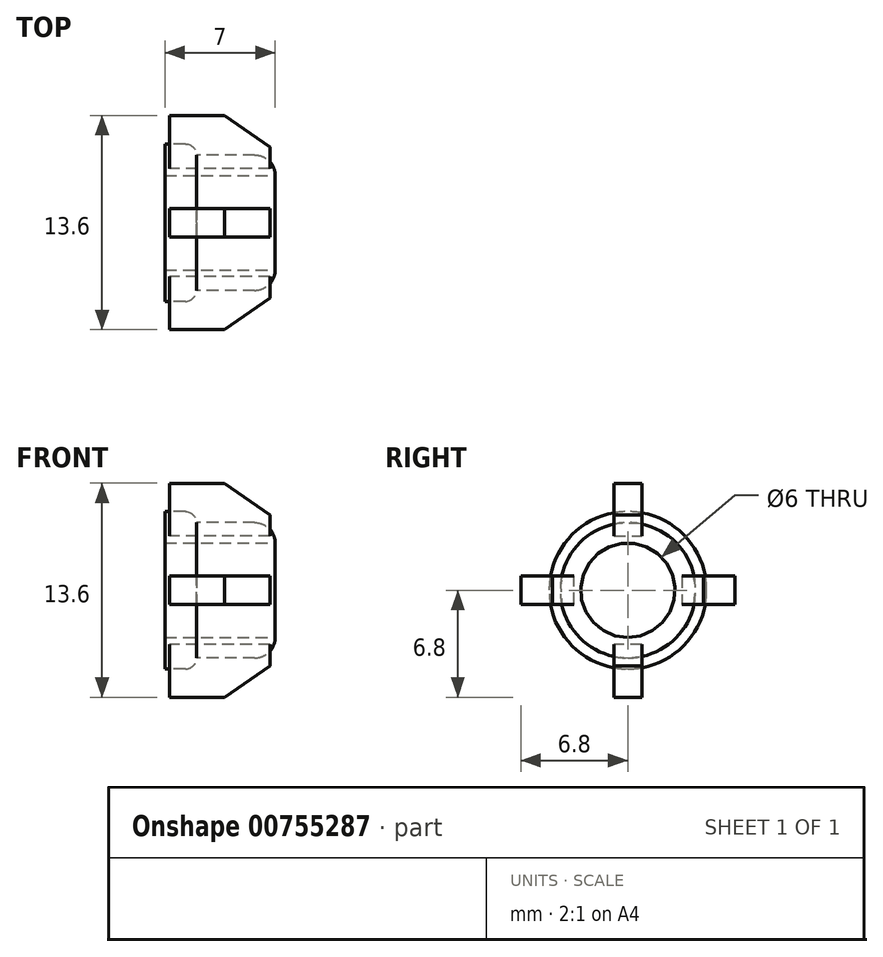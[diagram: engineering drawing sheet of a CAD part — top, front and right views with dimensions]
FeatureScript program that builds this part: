
annotation { "Feature Type Name" : "Feature", "Feature Type Description" : "" }
export const myFeature = defineFeature(function(context is Context, id is Id, definition is map)
    precondition{}
    {
        {
            var Q0;
            Q0=qCreatedBy(makeId("Right.planeOp"),FACE);
            var sketch = newSketch(context, id + "F0", { "sketchPlane" : qUnion([Q0])});
            skCircle(sketch, "E0", {"center": v(0, 0) * mm, "radius": 5 * mm});
            skSolve(sketch);
        }
        {
            var Q0;
            Q0=makeQuery(id+"F0.imprint","IMPRINT",FACE,{"disambiguationData":[TD([[makeQuery(id+"F0.imprint","IMPRINT",EDGE,{"derivedFrom":sQuery(id+"F0.wireOp",EDGE,"E0")}),1.0]])]});
            extrude(context, id + "F1", {"entities" : qUnion([Q0]), "depth" : 2 * mm, "offsetDistance" : 25 * mm});
        }
        {
            var Q0;
            Q0=makeQuery(id+"F1.opExtrude","CAP_FACE",FACE,{"disambiguationData":[OSD([sQuery(id+"F0.wireOp",EDGE,"E0")])],"isStart":false});
            fillet(context, id + "F2", {"entities" : qUnion([Q0]), "radius" : 0.7 * mm, "tangentPropagation" : true, "allowEdgeOverflow" : false});
        }
        {
            var Q0;
            Q0=makeQuery(id+"F1.opExtrude","CAP_FACE",FACE,{"disambiguationData":[OSD([sQuery(id+"F0.wireOp",EDGE,"E0")])],"isStart":false});
            var sketch = newSketch(context, id + "F3", { "sketchPlane" : qUnion([Q0])});
            skCircle(sketch, "E1", {"center": v(0, 0) * mm, "radius": 4.3 * mm});
            skSolve(sketch);
        }
        {
            var Q0;
            Q0=qSketchRegion(id+"F3",true);
            extrude(context, id + "F4", {"entities" : qUnion([Q0]), "operationType" : NewBodyOperationType.ADD, "depth" : 5 * mm, "offsetDistance" : 25 * mm});
        }
        {
            var Q0;
            Q0=makeQuery(id+"F4.opExtrude","CAP_FACE",FACE,{"disambiguationData":[OSD([sQuery(id+"F3.wireOp",EDGE,"E1")])],"isStart":false});
            fillet(context, id + "F5", {"entities" : qUnion([Q0]), "radius" : 1.3 * mm, "tangentPropagation" : true, "allowEdgeOverflow" : false});
        }
        {
            var Q0;
            Q0=makeQuery(id+"F4.opExtrude","CAP_FACE",FACE,{"disambiguationData":[OSD([sQuery(id+"F3.wireOp",EDGE,"E1")])],"isStart":false});
            var sketch = newSketch(context, id + "F6", { "sketchPlane" : qUnion([Q0])});
            skCircle(sketch, "E2", {"center": v(0, 0) * mm, "radius": 3 * mm});
            skSolve(sketch);
        }
        {
            var Q0;
            Q0=qSketchRegion(id+"F6",true);
            extrude(context, id + "F7", {"entities" : qUnion([Q0]), "operationType" : NewBodyOperationType.REMOVE, "oppositeDirection" : true, "depth" : 25 * mm, "offsetDistance" : 25 * mm});
        }
        {
            var Q0;
            Q0=qCreatedBy(makeId("Top.planeOp"),FACE);
            var sketch = newSketch(context, id + "F8", { "sketchPlane" : qUnion([Q0])});
            skLineSegment(sketch, "E3", {"start": v(0.28, 4.8) * mm, "end": v(0.28, 6.8) * mm});
            skLineSegment(sketch, "E4", {"start": v(0.28, 6.8) * mm, "end": v(3.78, 6.8) * mm});
            skLineSegment(sketch, "E5", {"start": v(3.78, 6.8) * mm, "end": v(6.68, 4.8) * mm});
            skLineSegment(sketch, "E6", {"start": v(6.68, 3.43) * mm, "end": v(0.28, 3.43) * mm});
            skLineSegment(sketch, "E7", {"start": v(6.68, 3.43) * mm, "end": v(6.68, 4.8) * mm});
            skLineSegment(sketch, "E8", {"start": v(0.28, 3.43) * mm, "end": v(0.28, 4.8) * mm});
            skSolve(sketch);
        }
        {
            var Q0;
            Q0=qSketchRegion(id+"F8",true);
            extrude(context, id + "F9", {"entities" : qUnion([Q0]), "endBound" : BoundingType.SYMMETRIC, "depth" : 1.8 * mm, "offsetDistance" : 25 * mm});
        }
        {
            var Q0;
            Q0=makeQuery(id+"F9.opExtrude","SWEPT_BODY",BODY,{"disambiguationData":[OSD([sQuery(id+"F8.wireOp",EDGE,"E3"),sQuery(id+"F8.wireOp",EDGE,"E4"),sQuery(id+"F8.wireOp",EDGE,"E5"),sQuery(id+"F8.wireOp",EDGE,"E6"),sQuery(id+"F8.wireOp",EDGE,"E7"),sQuery(id+"F8.wireOp",EDGE,"E8")])]});
            var Q1;
            Q1=makeQuery(id+"F4.opExtrude","SWEPT_FACE",FACE,{"disambiguationData":[OSD([sQuery(id+"F3.wireOp",EDGE,"E1")])]});
            circularPattern(context, id + "F10", {"entities" : qUnion([Q0]), "axis" : qUnion([Q1]), "angle" : 360 * degree, "instanceCount" : 4, "equalSpace" : true});
        }
    });
